# Revit family: Slink_Lounge_Chair_BIM
name_source: partatom
category: Arredi
units: mm (PartAtom-declared; Revit-internal decimal feet)

## family parameters
Attiva taglio nelle viste = No
Basato su piano di lavoro = No
Condiviso = No
Numero OmniClass = 23.40.20.00
Origine composizione di rendering = Geometria famiglia
Punto di calcolo locali = No
Sempre verticale = Sì
Taglio con vuoti quando caricato = No
Titolo OmniClass = General Furniture and Specialties

## types (1)
- CB-621
    AVAILABLE FINISHES = Ebonized black lacquer on Oak (EB). Raw effect lacquer on Oak (RE). Hand rubbed natural oil on Oak or Walnut (NA), or hand rubbed black oil on Walnut (BO).
    BASE MATERIAL = BASSAM_FELLOWS_ELEGANT_LEATHER_48027_OLIVE
    BIM BADGE = https://bim.archiproducts.com
    COLLECTION = Slink
    DEPTH = 666 mm  [stored 2.18504 ft]
    Descrizione = Upholstered solid wood lounge chair
    FEET MATERIAL = BASSAM_FELLOWS_WALNUT
    HEIGHT = 748 mm  [stored 2.45407 ft]
    MATERIAL DESCRIPTION = Carved solid wood base. Foam upholstery. Carved CARB2 plywood inner shell. Welt detail.
    Modello = Slink Lounge Chair
    PRODUCT CODE = CB-621
    PRODUCT SHEET = https://www.archiproducts.com
    Produttore = BassamFellows
    Prospetto di default = 0 mm  [stored 0 ft]
    TECHNICAL SHEET = https://bassamfellows.com
    URL = https://bassamfellows.com
    WIDTH = 588 mm  [stored 1.92913 ft]

note: [stored X ft] marks values corroborated as IEEE doubles in the binary element streams (Revit-internal decimal feet)

## geometry (parser evidence)
native form markers: Sweep x2
no freeform markers — native parametric forms only
